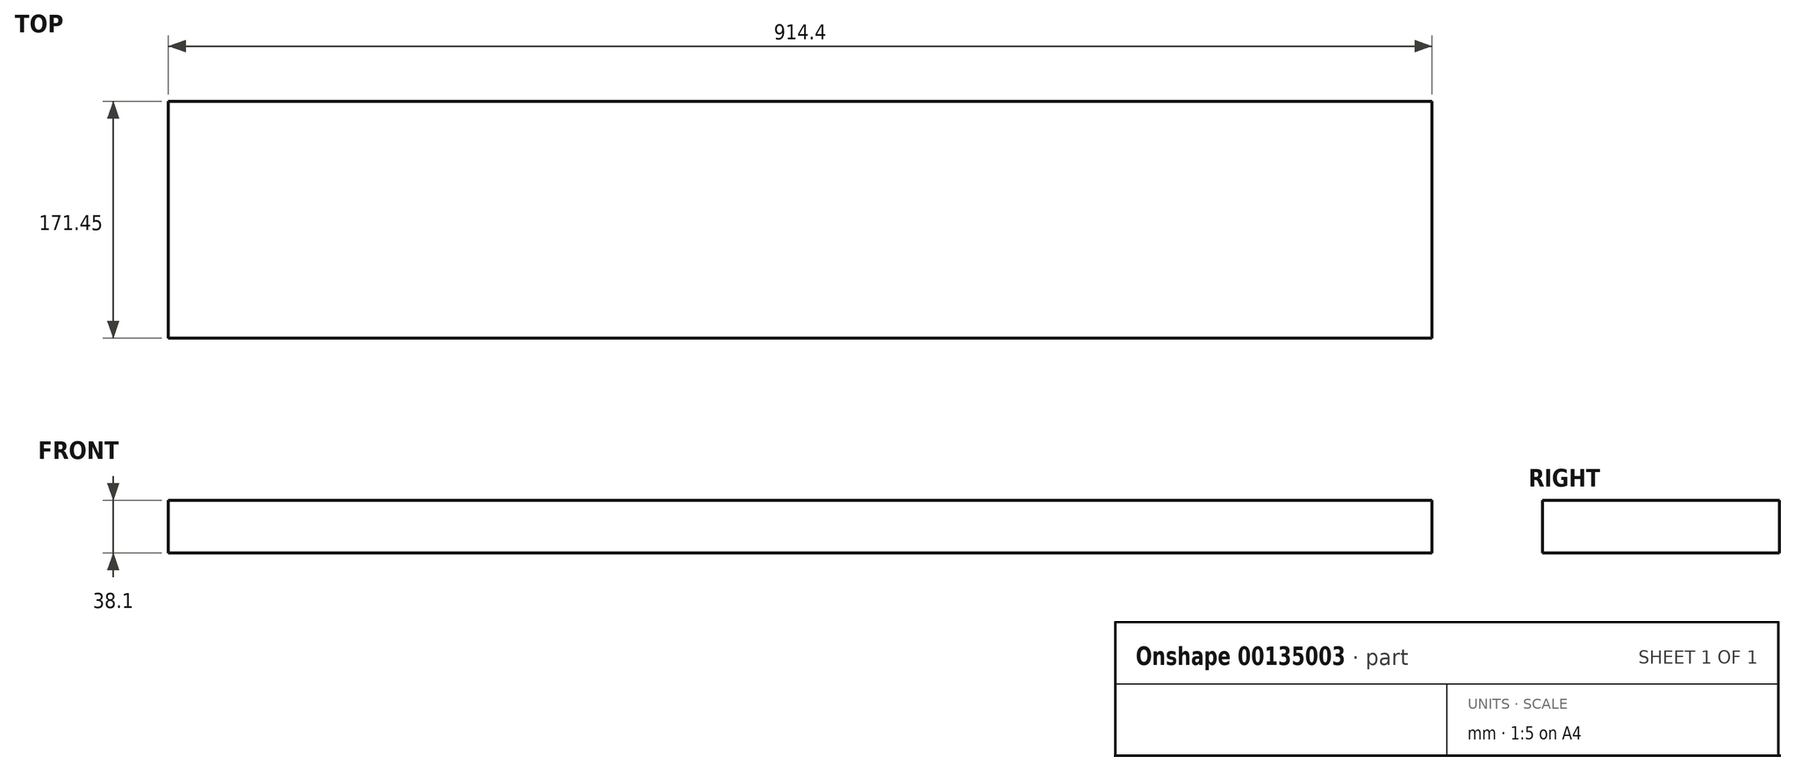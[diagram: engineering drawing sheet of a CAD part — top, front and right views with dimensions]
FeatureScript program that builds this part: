
annotation { "Feature Type Name" : "Feature", "Feature Type Description" : "" }
export const myFeature = defineFeature(function(context is Context, id is Id, definition is map)
    precondition{}
    {
        {
            var Q0;
            Q0=qCreatedBy(makeId("Right.planeOp"),FACE);
            var sketch = newSketch(context, id + "F0", { "sketchPlane" : qUnion([Q0])});
            skLineSegment(sketch, "E0.bottom", {"start": v(0, 0) * mm, "end": v(171.45, 0) * mm});
            skLineSegment(sketch, "E0.top", {"start": v(0, 38.1) * mm, "end": v(171.45, 38.1) * mm});
            skLineSegment(sketch, "E0.left", {"start": v(0, 0) * mm, "end": v(0, 38.1) * mm});
            skLineSegment(sketch, "E0.right", {"start": v(171.45, 0) * mm, "end": v(171.45, 38.1) * mm});
            skSolve(sketch);
        }
        {
            var Q0;
            Q0=makeQuery(id+"F0.imprint","IMPRINT",FACE,{"disambiguationData":[TD([[makeQuery(id+"F0.imprint","IMPRINT",EDGE,{"derivedFrom":sQuery(id+"F0.wireOp",EDGE,"E0.bottom")}),1.0]])]});
            extrude(context, id + "F1", {"entities" : qUnion([Q0]), "depth" : 914.4 * mm});
        }
    });
